# Revit family: Lavatory_System-Wall_Mount-Trueform_Concrete-Single_Ramp_Basin-Configurable_1_or_2_Station
name_source: partatom
category: Plumbing Fixtures
revit_build: Autodesk Revit LT 2015 (Build: 20140606_1530(x64)
units: mm (PartAtom-declared; Revit-internal decimal feet)

## types (6) — shared parameters
AHC = 5"
Apron Height = 5"
Basin Height = 5"
Basin/Countertop Reconciliation Warning = No
Bracket Placement Warning = No
Brackets = Steel, Paint Finish, Dark Gray, Matte
Lavatory = GFRC - Concrete
Manufacturer = Trueform Concrete
Non Standard Sink Basin Model Note = No
RLAC = 1/8"
RRAC = 1/8"
Remove Left Apron = No
Remove Right Apron = No
Tailpiece = Polished Chrome
URL = https://www.trueformconcrete.com
Use Left Bracket = Yes
Use Right Bracket = Yes
Vent Connection = No
Verify Rear Countertop = 5"
Waste Connection = Yes

## per-type parameters (varying)
- R-1812: Additional Support Required Note=No; BDC=17"; BSC=2"; Basin Center to Countertop Edge MIN=12"; Basin Center to Left Countertop Edge=12"; Basin Center to Right Countertop Edge=12"; Basin Depth=12"; Basin Front Setback=2"; Basin Front Setback Max=5"; Basin ID (Do not edit value)=1812; Basin Length=18"; CWFU=0.5; Description=Wall-mount GFRC Single Station Ramp Basin Lavatory; HWFU=0.5; LCC=12"; Left Bracket - L=Yes; Left Bracket - T=No; Left Bracket to Basin Center=10 1/2"; Left Bracket to Basin Center MAX=10 1/2"; Left Bracket to Basin Center MIN=10 1/2"; Model=FLO-24V-ADA; ODC=19"; Overall Countertop Depth=19"; Overall Countertop Depth MIN=14"; Overall Countertop Length=24"; Overall Countertop Length MIN=24"; RCC=12"; Right Bracket - L=Yes; Right Bracket - T=No; Right Bracket to Basin Center=10 1/2"; Right Bracket to Basin Center MAX=10 1/2"; Right Bracket to Basin Center MIN=10 1/2"; SDC=1/4"; Verify Basin Center to Left Countertop Edge=12"; Verify Basin Center to Right Countertop Edge=12"; Verify Basin Front Setback=2"; Verify Left Bracket Placement=10 1/2"; Verify Overall Countertop Depth=19"; Verify Overall Countertop Length=24"; Verify Right Bracket Placement=10 1/2"; WFU=1; Waste Fitting=1 1/4"
- R-2013: Additional Support Required Note=No; BDC=19"; BSC=3"; Basin Center to Countertop Edge MIN=13"; Basin Center to Left Countertop Edge=15"; Basin Center to Right Countertop Edge=15"; Basin Depth=13"; Basin Front Setback=3"; Basin Front Setback Max=6"; Basin ID (Do not edit value)=2013; Basin Length=20"; CWFU=0.5; Description=Wall-mount GFRC Single Station Ramp Basin Lavatory; HWFU=0.5; LCC=15"; Left Bracket - L=Yes; Left Bracket - T=No; Left Bracket to Basin Center=12 1/2"; Left Bracket to Basin Center MAX=13 1/2"; Left Bracket to Basin Center MIN=11 1/2"; Model=FLO-30V-ADA; ODC=21"; Overall Countertop Depth=21"; Overall Countertop Depth MIN=15"; Overall Countertop Length=30"; Overall Countertop Length MIN=26"; RCC=15"; Right Bracket - L=Yes; Right Bracket - T=No; Right Bracket to Basin Center=12 1/2"; Right Bracket to Basin Center MAX=13 1/2"; Right Bracket to Basin Center MIN=11 1/2"; SDC=1/4"; Verify Basin Center to Left Countertop Edge=15"; Verify Basin Center to Right Countertop Edge=15"; Verify Basin Front Setback=3"; Verify Left Bracket Placement=12 1/2"; Verify Overall Countertop Depth=21"; Verify Overall Countertop Length=30"; Verify Right Bracket Placement=12 1/2"; WFU=1; Waste Fitting=1 1/4"
- R-1410: Additional Support Required Note=No; BDC=15"; BSC=2"; Basin Center to Countertop Edge MIN=10"; Basin Center to Left Countertop Edge=10"; Basin Center to Right Countertop Edge=10"; Basin Depth=10"; Basin Front Setback=2"; Basin Front Setback Max=5"; Basin ID (Do not edit value)=1410; Basin Length=14"; CWFU=0.5; Description=Wall-mount GFRC Single Station Ramp Basin Lavatory; HWFU=0.5; LCC=10"; Left Bracket - L=Yes; Left Bracket - T=No; Left Bracket to Basin Center=8 1/2"; Left Bracket to Basin Center MAX=8 1/2"; Left Bracket to Basin Center MIN=8 1/2"; Model=FLO-20V-ADA; ODC=17"; Overall Countertop Depth=17"; Overall Countertop Depth MIN=12"; Overall Countertop Length=20"; Overall Countertop Length MIN=20"; RCC=10"; Right Bracket - L=Yes; Right Bracket - T=No; Right Bracket to Basin Center=8 1/2"; Right Bracket to Basin Center MAX=8 1/2"; Right Bracket to Basin Center MIN=8 1/2"; SDC=1/4"; Verify Basin Center to Left Countertop Edge=10"; Verify Basin Center to Right Countertop Edge=10"; Verify Basin Front Setback=2"; Verify Left Bracket Placement=8 1/2"; Verify Overall Countertop Depth=17"; Verify Overall Countertop Length=20"; Verify Right Bracket Placement=8 1/2"; WFU=1; Waste Fitting=1 1/4"
- R-4813: Additional Support Required Note=No; BDC=19"; BSC=3"; Basin Center to Countertop Edge MIN=27"; Basin Center to Left Countertop Edge=30"; Basin Center to Right Countertop Edge=30"; Basin Depth=13"; Basin Front Setback=3"; Basin Front Setback Max=6"; Basin ID (Do not edit value)=4813; Basin Length=48"; CWFU=1; Description=Wall-mount GFRC 2 Station Ramp Basin Lavatory; HWFU=1; LCC=30"; Left Bracket - L=No; Left Bracket - T=Yes; Left Bracket to Basin Center=27"; Left Bracket to Basin Center MAX=28 1/2"; Left Bracket to Basin Center MIN=25 1/2"; Model=FLO-60V-ADA; ODC=21"; Overall Countertop Depth=21"; Overall Countertop Depth MIN=15"; Overall Countertop Length=60"; Overall Countertop Length MIN=54"; RCC=30"; Right Bracket - L=No; Right Bracket - T=Yes; Right Bracket to Basin Center=27"; Right Bracket to Basin Center MAX=28 1/2"; Right Bracket to Basin Center MIN=25 1/2"; SDC=1/2"; Verify Basin Center to Left Countertop Edge=30"; Verify Basin Center to Right Countertop Edge=30"; Verify Basin Front Setback=3"; Verify Left Bracket Placement=27"; Verify Overall Countertop Depth=21"; Verify Overall Countertop Length=60"; Verify Right Bracket Placement=27"; WFU=3; Waste Fitting=1 1/2"
- R-6013: Additional Support Required Note=No; BDC=19"; BSC=3"; Basin Center to Countertop Edge MIN=33"; Basin Center to Left Countertop Edge=36"; Basin Center to Right Countertop Edge=36"; Basin Depth=13"; Basin Front Setback=3"; Basin Front Setback Max=6"; Basin ID (Do not edit value)=6013; Basin Length=60"; CWFU=1.5; Description=Wall-mount GFRC 2 or 3 Station Ramp Basin Lavatory; HWFU=1.5; LCC=36"; Left Bracket - L=No; Left Bracket - T=Yes; Left Bracket to Basin Center=33"; Left Bracket to Basin Center MAX=34 1/2"; Left Bracket to Basin Center MIN=31 1/2"; Model=FLO-72V-ADA; ODC=21"; Overall Countertop Depth=21"; Overall Countertop Depth MIN=15"; Overall Countertop Length=72"; Overall Countertop Length MIN=66"; RCC=36"; Right Bracket - L=No; Right Bracket - T=Yes; Right Bracket to Basin Center=33"; Right Bracket to Basin Center MAX=34 1/2"; Right Bracket to Basin Center MIN=31 1/2"; SDC=5/8"; Verify Basin Center to Left Countertop Edge=36"; Verify Basin Center to Right Countertop Edge=36"; Verify Basin Front Setback=3"; Verify Left Bracket Placement=33"; Verify Overall Countertop Depth=21"; Verify Overall Countertop Length=72"; Verify Right Bracket Placement=33"; WFU=3; Waste Fitting=1 1/2"
- R-7213: Additional Support Required Note=Yes; BDC=19"; BSC=3"; Basin Center to Countertop Edge MIN=39"; Basin Center to Left Countertop Edge=42"; Basin Center to Right Countertop Edge=42"; Basin Depth=13"; Basin Front Setback=3"; Basin Front Setback Max=6"; Basin ID (Do not edit value)=7213; Basin Length=72"; CWFU=1.5; Description=Wall-mount GFRC 2 or 3 Station Ramp Basin Lavatory; HWFU=1.5; LCC=42"; Left Bracket - L=No; Left Bracket - T=Yes; Left Bracket to Basin Center=39"; Left Bracket to Basin Center MAX=40 1/2"; Left Bracket to Basin Center MIN=37 1/2"; Model=Custom Lavatory; ODC=21"; Overall Countertop Depth=21"; Overall Countertop Depth MIN=15"; Overall Countertop Length=84"; Overall Countertop Length MIN=78"; RCC=42"; Right Bracket - L=No; Right Bracket - T=Yes; Right Bracket to Basin Center=39"; Right Bracket to Basin Center MAX=40 1/2"; Right Bracket to Basin Center MIN=37 1/2"; SDC=3/4"; Verify Basin Center to Left Countertop Edge=42"; Verify Basin Center to Right Countertop Edge=42"; Verify Basin Front Setback=3"; Verify Left Bracket Placement=39"; Verify Overall Countertop Depth=21"; Verify Overall Countertop Length=84"; Verify Right Bracket Placement=39"; WFU=3; Waste Fitting=1 1/2"

## geometry (parser evidence)
native form markers: Sweep x6
no freeform markers — native parametric forms only
